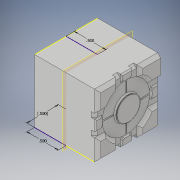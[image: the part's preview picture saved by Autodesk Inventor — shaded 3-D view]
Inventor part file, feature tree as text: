
AUTODESK INVENTOR PART (.ipt)
format: ipt  version: 2018 (Build 220112000, 112)  size: 616,960 bytes
history: native  units: in
note: dims shown in document units (in); Inventor stores cm internally (conversion verified against a paired STEP export)
features: chamfer x51, sketch x11, extrude x9, plane x1
ambient origin geometry x8: Origin, YZ Plane, XZ Plane, XY Plane, X Axis, Y Axis, Z Axis, Center Point
bodies: Solid1 (feature_tree)
feature tree (72):
  extrude  "Extrusion1"  Depth=1.0in
  extrude  "Extrusion2"  Depth=0.333in
  extrude  "Extrusion3"  Depth=0.333in
  chamfer  "Chamfer20"  Distance=0.05in
  chamfer  "Chamfer21"  Distance=0.02in
  chamfer  "Chamfer22"  Distance=0.05in Angle=45.0deg
  chamfer  "Chamfer23"  Distance=0.05in Angle=45.0deg
  chamfer  "Chamfer24"  Distance=0.05in Angle=45.0deg
  chamfer  "Chamfer25"  Distance=0.05in Angle=45.0deg
  chamfer  "Chamfer26"  Distance=0.05in Angle=45.0deg
  chamfer  "Chamfer27"  Distance=0.05in Angle=45.0deg
  chamfer  "Chamfer28"  Distance=0.05in Angle=45.0deg
  chamfer  "Chamfer30"  Distance=0.05in Angle=45.0deg
  chamfer  "Chamfer31"  Distance=0.05in Angle=45.0deg
  chamfer  "Chamfer32"  Distance=0.05in Angle=45.0deg
  chamfer  "Chamfer33"  Distance=0.05in Angle=45.0deg
  chamfer  "Chamfer34"  Distance=0.05in Angle=45.0deg
  chamfer  "Chamfer35"  Distance=0.05in Angle=45.0deg
  chamfer  "Chamfer36"  Distance=0.05in Angle=45.0deg
  chamfer  "Chamfer37"  Distance=0.05in Angle=45.0deg
  chamfer  "Chamfer38"  Distance=0.05in Angle=45.0deg
  chamfer  "Chamfer39"  Distance=0.05in Angle=45.0deg
  chamfer  "Chamfer40"  Distance=0.05in Angle=45.0deg
  chamfer  "Chamfer41"  Distance=0.05in Angle=45.0deg
  chamfer  "Chamfer42"  Distance=0.05in Angle=45.0deg
  chamfer  "Chamfer43"  Distance=0.05in Angle=45.0deg
  chamfer  "Chamfer44"  Distance=0.02in Angle=45.0deg
  chamfer  "Chamfer45"  Distance=0.02in Angle=45.0deg
  chamfer  "Chamfer46"  Distance=0.02in Angle=45.0deg
  chamfer  "Chamfer47"  Distance=0.02in Angle=45.0deg
  chamfer  "Chamfer48"  Distance=0.02in Angle=45.0deg
  chamfer  "Chamfer49"  Distance=0.02in Angle=45.0deg
  chamfer  "Chamfer50"  Distance=0.02in Angle=45.0deg
  chamfer  "Chamfer51"  Distance=0.02in Angle=45.0deg
  chamfer  "Chamfer52"  Distance=0.02in Angle=45.0deg
  chamfer  "Chamfer53"  Distance=0.02in Angle=45.0deg
  extrude  "Extrusion4"  Depth=0.02in TaperAngle=45.0deg
  chamfer  "Chamfer54"  Distance=0.75in
  chamfer  "Chamfer55"  Distance=0.05in
  chamfer  "Chamfer56"  Distance=0.05in Angle=45.0deg
  chamfer  "Chamfer57"  Distance=0.05in Angle=45.0deg
  chamfer  "Chamfer58"  Distance=0.05in Angle=45.0deg
  chamfer  "Chamfer59"  Distance=0.05in Angle=45.0deg
  chamfer  "Chamfer60"  Distance=0.02in Angle=45.0deg
  chamfer  "Chamfer61"  Distance=0.02in Angle=45.0deg
  chamfer  "Chamfer62"  Distance=0.02in Angle=45.0deg
  chamfer  "Chamfer63"  Distance=0.02in Angle=45.0deg
  chamfer  "Chamfer64"  Distance=0.02in Angle=45.0deg
  chamfer  "Chamfer65"  Distance=0.02in Angle=45.0deg
  chamfer  "Chamfer66"  Distance=0.02in Angle=45.0deg
  chamfer  "Chamfer67"  Distance=0.02in Angle=45.0deg
  chamfer  "Chamfer68"  Distance=0.02in Angle=45.0deg
  chamfer  "Chamfer69"  Distance=0.02in Angle=45.0deg
  extrude  "Extrusion5"  Depth=0.02in TaperAngle=45.0deg
  chamfer  "Chamfer70"  Distance=0.02in Angle=45.0deg
  extrude  "Extrusion6"  Depth=0.005in
  extrude  "Extrusion7"  Depth=0.005in TaperAngle=0.0deg
  chamfer  "Chamfer71"  Distance=0.375in Angle=45.0deg
  extrude  "Extrusion8"  Depth=0.005in
  extrude  "Extrusion9"  Depth=0.005in
  sketch  "Sketch13"  dims[d66=0.08in d67=0.02in d68=0.0in d75=0.05in d76=0.05in d77=45.0deg d78=0.05in d79=0.05in d80=45.0deg d81=0.05in d82=0.05in d83=45.0deg d84=0.05in d85=0.05in d86=45.0deg d87=0.05in d88=0.05in d89=45.0deg d90=0.05in d91=0.05in d92=45.0deg d93=0.05in d94=0.05in d95=45.0deg d96=0.05in d97=0.05in d98=45.0deg d99=0.05in d100=0.05in d101=45.0deg d105=0.05in d106=0.05in d107=45.0deg d108=0.05in d109=0.05in d110=45.0deg d111=0.05in d112=0.05in d113=45.0deg d114=0.05in d115=0.05in d116=45.0deg d117=0.05in d118=0.05in d119=45.0deg d120=0.05in d121=0.05in d122=45.0deg d123=0.05in d124=0.05in d125=45.0deg d126=0.05in d127=0.05in d128=45.0deg d129=0.05in d130=0.05in d131=45.0deg d132=0.05in d133=0.05in d134=45.0deg d135=0.05in d136=0.05in d137=45.0deg d138=0.05in d139=0.05in d140=45.0deg d141=0.02in d142=0.02in d143=45.0deg d144=0.02in d145=0.02in d146=45.0deg d147=0.02in d148=0.02in d149=45.0deg d150=0.02in d151=0.02in d152=45.0deg d153=0.02in d154=0.02in d155=45.0deg d156=0.02in d157=0.02in d158=45.0deg d159=0.02in d160=0.02in d161=45.0deg d162=0.02in d163=0.02in d164=45.0deg d165=0.02in d166=0.02in d167=45.0deg d168=0.02in d169=0.02in d170=45.0deg]
  sketch  "Sketch14"  dims[d171=0.02in d172=0.02in d173=45.0deg d174=0.02in d175=0.02in d176=45.0deg d177=0.75in d178=0.05in d179=0.0in d180=0.05in d181=0.05in d182=45.0deg d183=0.05in d184=0.05in d185=45.0deg d186=0.05in d187=0.05in d188=45.0deg d189=0.05in d190=0.05in d191=45.0deg d192=0.02in d193=0.02in d194=45.0deg d195=0.02in d196=0.02in d197=45.0deg d198=0.02in d199=0.02in d200=45.0deg d201=0.02in d202=0.02in d203=45.0deg d204=0.02in d205=0.02in d206=45.0deg d207=0.02in d208=0.02in d209=45.0deg d210=0.02in d211=0.02in d212=45.0deg d213=0.02in d214=0.02in d215=45.0deg d216=0.02in d217=0.02in d218=45.0deg d220=0.02in d221=0.02in d222=45.0deg d223=0.02in d224=0.02in d225=45.0deg d226=0.02in d227=0.02in d228=45.0deg d229=0.75in d230=0.01in d231=0.0in d232=0.375in d233=0.01in d234=45.0deg d239=0.49in d240=0.49in d241=0.02in d242=0.02in d243=1.0in d244=0.01in d245=0.0in d246=0.5in d247=0.5in d248=0.4in d249=0.03in d250=0.0in d251=0.01in d252=0.03in d253=45.0deg d254=0.36in d255=0.005in d256=0.0in d257=0.01in d258=0.0in d260=0.5in d261=0.5in d262=0.5in d263=0.5in]
  plane  "Work Plane3"
  sketch  "Sketch1"  dims[d0=1.0in d1=1.0in]
  sketch  "Sketch2"  dims[d2=1.0in d3=0.0in d4=0.333in]
  sketch  "Sketch3"  dims[d5=0.333in d6=0.333in]
  sketch  "Sketch4"  dims[d7=0.333in]
  sketch  "Sketch6"  dims[d8=0.333in]
  sketch  "Sketch8"  dims[d9=0.333in d10=0.05in d11=0.0in]
  sketch  "Sketch9"  dims[d63=0.08in]
  sketch  "Sketch10"  dims[d64=0.08in]
  sketch  "Sketch12"  dims[d65=0.08in]
